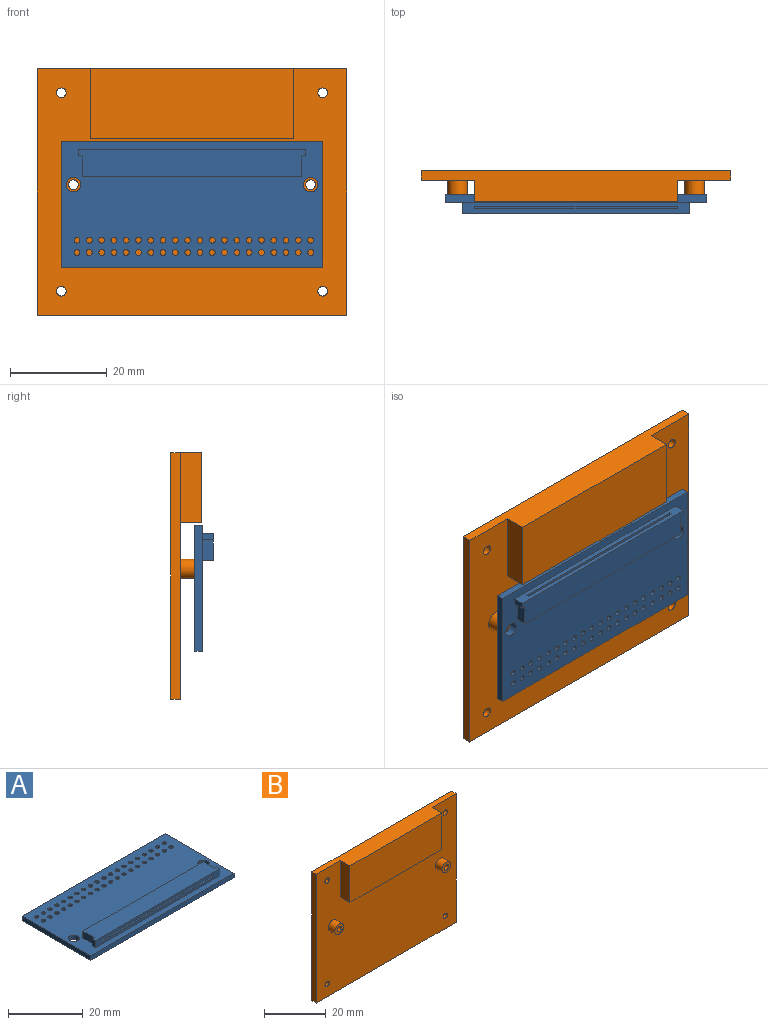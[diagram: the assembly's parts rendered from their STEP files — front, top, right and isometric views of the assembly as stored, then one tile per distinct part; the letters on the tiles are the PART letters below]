
ASSEMBLY  parts=2 mates=1
PART A: 62 faces, bbox 54x26x3.8 mm
  f0: plane 47x2.3mm, normal (0,-1,0), area 87.2mm2, adj f1,f53,f54,f56,f57,f58,f59,f60
  f1: plane 54x26mm, normal (0,0,1), area 1092.9mm2, adj f0,f2,f3,f4,f5,f6,f7,f8
  f2: plane 54x1.5mm, normal (0,-1,0), area 81mm2, adj f1,f3,f47,f48
  f3: plane 26x1.5mm, normal (1,0,0), area 39mm2, adj f1,f2,f4,f48
  f4: plane 54x1.5mm, normal (0,1,0), area 81mm2, adj f1,f3,f47,f48
  f5: cylinder r=0.6mm len=1.5mm, axis (0,0,-1), area 5.7mm2, adj f1,f48
  f6: cylinder r=0.6mm len=1.5mm, axis (0,0,-1), area 5.7mm2, adj f1,f48
  f7: cylinder r=0.6mm len=1.5mm, axis (0,0,-1), area 5.7mm2, adj f1,f48
  f8: cylinder r=0.6mm len=1.5mm, axis (0,0,-1), area 5.7mm2, adj f1,f48
  f9: cylinder r=0.6mm len=1.5mm, axis (0,0,-1), area 5.7mm2, adj f1,f48
  f10: cylinder r=0.6mm len=1.5mm, axis (0,0,-1), area 5.7mm2, adj f1,f48
  f11: cylinder r=0.6mm len=1.5mm, axis (0,0,-1), area 5.7mm2, adj f1,f48
  f12: cylinder r=0.6mm len=1.5mm, axis (0,0,-1), area 5.7mm2, adj f1,f48
  f13: cylinder r=0.6mm len=1.5mm, axis (0,0,-1), area 5.7mm2, adj f1,f48
  f14: cylinder r=0.6mm len=1.5mm, axis (0,0,-1), area 5.7mm2, adj f1,f48
  f15: cylinder r=0.6mm len=1.5mm, axis (0,0,-1), area 5.7mm2, adj f1,f48
  f16: cylinder r=0.6mm len=1.5mm, axis (0,0,-1), area 5.7mm2, adj f1,f48
  f17: cylinder r=0.6mm len=1.5mm, axis (0,0,-1), area 5.7mm2, adj f1,f48
  f18: cylinder r=0.6mm len=1.5mm, axis (0,0,-1), area 5.7mm2, adj f1,f48
  f19: cylinder r=0.6mm len=1.5mm, axis (0,0,-1), area 5.7mm2, adj f1,f48
  f20: cylinder r=0.6mm len=1.5mm, axis (0,0,-1), area 5.7mm2, adj f1,f48
  f21: cylinder r=0.6mm len=1.5mm, axis (0,0,-1), area 5.7mm2, adj f1,f48
  f22: cylinder r=0.6mm len=1.5mm, axis (0,0,-1), area 5.7mm2, adj f1,f48
  f23: cylinder r=0.6mm len=1.5mm, axis (0,0,-1), area 5.7mm2, adj f1,f48
  f24: cylinder r=0.6mm len=1.5mm, axis (0,0,-1), area 5.7mm2, adj f1,f48
  f25: cylinder r=0.6mm len=1.5mm, axis (0,0,-1), area 5.7mm2, adj f1,f48
  f26: cylinder r=0.6mm len=1.5mm, axis (0,0,-1), area 5.7mm2, adj f1,f48
  f27: cylinder r=0.6mm len=1.5mm, axis (0,0,-1), area 5.7mm2, adj f1,f48
  f28: cylinder r=0.6mm len=1.5mm, axis (0,0,-1), area 5.7mm2, adj f1,f48
  f29: cylinder r=0.6mm len=1.5mm, axis (0,0,-1), area 5.7mm2, adj f1,f48
  f30: cylinder r=0.6mm len=1.5mm, axis (0,0,-1), area 5.7mm2, adj f1,f48
  f31: cylinder r=0.6mm len=1.5mm, axis (0,0,-1), area 5.7mm2, adj f1,f48
  f32: cylinder r=0.6mm len=1.5mm, axis (0,0,-1), area 5.7mm2, adj f1,f48
  f33: cylinder r=0.6mm len=1.5mm, axis (0,0,-1), area 5.7mm2, adj f1,f48
  f34: cylinder r=0.6mm len=1.5mm, axis (0,0,-1), area 5.7mm2, adj f1,f48
  f35: cylinder r=0.6mm len=1.5mm, axis (0,0,-1), area 5.7mm2, adj f1,f48
  f36: cylinder r=0.6mm len=1.5mm, axis (0,0,-1), area 5.7mm2, adj f1,f48
  f37: cylinder r=0.6mm len=1.5mm, axis (0,0,-1), area 5.7mm2, adj f1,f48
  f38: cylinder r=0.6mm len=1.5mm, axis (0,0,-1), area 5.7mm2, adj f1,f48
  f39: cylinder r=0.6mm len=1.5mm, axis (0,0,-1), area 5.7mm2, adj f1,f48
  f40: cylinder r=0.6mm len=1.5mm, axis (0,0,-1), area 5.7mm2, adj f1,f48
  f41: cylinder r=0.6mm len=1.5mm, axis (0,0,-1), area 5.7mm2, adj f1,f48
  f42: cylinder r=0.6mm len=1.5mm, axis (0,0,-1), area 5.7mm2, adj f1,f48
  f43: cylinder r=0.6mm len=1.5mm, axis (0,0,-1), area 5.7mm2, adj f1,f48
  f44: cylinder r=0.6mm len=1.5mm, axis (0,0,-1), area 5.7mm2, adj f1,f48
  f45: cylinder r=1.5mm len=3mm, axis (0,0,-1), area 14.1mm2, adj f1,f48
  f46: cylinder r=1.5mm len=3mm, axis (0,0,-1), area 14.1mm2, adj f1,f48
  f47: plane 26x1.5mm, normal (-1,0,0), area 39mm2, adj f1,f2,f4,f48
  f48: plane 54x26mm, normal (0,0,-1), area 1344.6mm2, adj f2,f3,f4,f5,f6,f7,f8,f9
  f49: plane 4.25x2.3mm, normal (1,0,0), area 9.8mm2, adj f1,f50,f55,f56
  f50: plane 45.4x2.3mm, normal (0,1,0), area 104.4mm2, adj f1,f49,f51,f56
  f51: plane 4.25x2.3mm, normal (-1,0,0), area 9.8mm2, adj f1,f50,f52,f56
  f52: plane 2.3x0.8mm, normal (0,1,0), area 1.8mm2, adj f1,f51,f53,f56
  f53: plane 2.3x1.25mm, normal (-1,0,0), area 2.9mm2, adj f0,f1,f52,f56
  f54: plane 2.3x1.25mm, normal (1,0,0), area 2.9mm2, adj f0,f1,f55,f56
  f55: plane 2.3x0.8mm, normal (0,1,0), area 1.8mm2, adj f1,f49,f54,f56
  f56: plane 47x5.5mm, normal (0,0,1), area 251.7mm2, adj f0,f49,f50,f51,f52,f53,f54,f55
  f57: plane 41.8x4mm, normal (0,0,1), area 167.2mm2, adj f0,f58,f60,f61
  f58: plane 4x0.5mm, normal (-1,0,0), area 2mm2, adj f0,f57,f59,f61
  f59: plane 41.8x4mm, normal (0,0,-1), area 167.2mm2, adj f0,f58,f60,f61
  f60: plane 4x0.5mm, normal (1,0,0), area 2mm2, adj f0,f57,f59,f61
  f61: plane 41.8x0.5mm, normal (0,-1,0), area 20.9mm2, adj f57,f58,f59,f60
PART B: 20 faces, bbox 64x6.4x51 mm
  f0: plane 64x51mm, normal (0,-1,0), area 2617.3mm2, adj f1,f2,f3,f5,f6,f7,f8,f10
  f1: plane 64x6.4mm, normal (0,0,1), area 312.8mm2, adj f0,f2,f10,f11,f17,f18,f19
  f2: plane 51x2mm, normal (-1,0,0), area 102mm2, adj f0,f1,f3,f11
  f3: plane 64x2mm, normal (0,0,-1), area 128mm2, adj f0,f2,f10,f11
  f4: cylinder r=1mm len=5mm, axis (0,-1,0), area 31.4mm2, adj f11,f13
  f5: cylinder r=1mm len=2mm, axis (0,-1,0), area 12.6mm2, adj f0,f11
  f6: cylinder r=1mm len=2mm, axis (0,-1,0), area 12.6mm2, adj f0,f11
  f7: cylinder r=1mm len=2mm, axis (0,-1,0), area 12.6mm2, adj f0,f11
  f8: cylinder r=1mm len=2mm, axis (0,-1,0), area 12.6mm2, adj f0,f11
  f9: cylinder r=1mm len=5mm, axis (0,-1,0), area 31.4mm2, adj f11,f15
  f10: plane 51x2mm, normal (1,0,0), area 102mm2, adj f0,f1,f3,f11
  f11: plane 64x51mm, normal (0,1,0), area 3245.2mm2, adj f1,f2,f3,f4,f5,f6,f7,f8
  f12: cylinder r=2mm len=4mm, axis (0,1,0), area 37.7mm2, adj f0,f13
  f13: plane 4x4mm, normal (0,-1,0), area 9.4mm2, adj f4,f12
  f14: cylinder r=2mm len=4mm, axis (0,1,0), area 37.7mm2, adj f0,f15
  f15: plane 4x4mm, normal (0,-1,0), area 9.4mm2, adj f9,f14
  f16: plane 42x4.4mm, normal (0,0,-1), area 184.8mm2, adj f0,f17,f18,f19
  f17: plane 14.5x4.4mm, normal (1,0,0), area 63.8mm2, adj f0,f1,f16,f19
  f18: plane 14.5x4.4mm, normal (-1,0,0), area 63.8mm2, adj f0,f1,f16,f19
  f19: plane 42x14.5mm, normal (0,-1,0), area 609mm2, adj f1,f16,f17,f18
PLACE A rot(axis=(0,0.71,-0.71),180deg) t=(0,-3,0)mm
PLACE B at identity fixed
MATE fastened A.f45 <-> B.f9  axis (0,1,0) through (24.5,-3,4)mm
